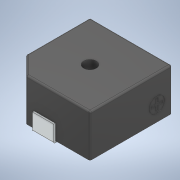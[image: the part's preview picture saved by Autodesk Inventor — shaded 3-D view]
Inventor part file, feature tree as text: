
AUTODESK INVENTOR PART (.ipt)
format: ipt  version: 2020 (Build 240168000, 168)  size: 197,120 bytes
history: native  units: mm
features: extrude x1, sketch x1, other x1
ambient origin geometry x8: Origin, YZ Plane, XZ Plane, XY Plane, X Axis, Y Axis, Z Axis, Center Point
bodies: Solid1 (feature_tree)
feature tree (3):
  extrude  "Extrusion1"  Depth=1.0mm
  sketch  "Sketch1"  dims[d0=1.0mm d1=0.0mm d2=0.5mm d3=0.872665mm d4=0.5mm d5=0.872665mm]
  other  "Cut-Extrude2"
